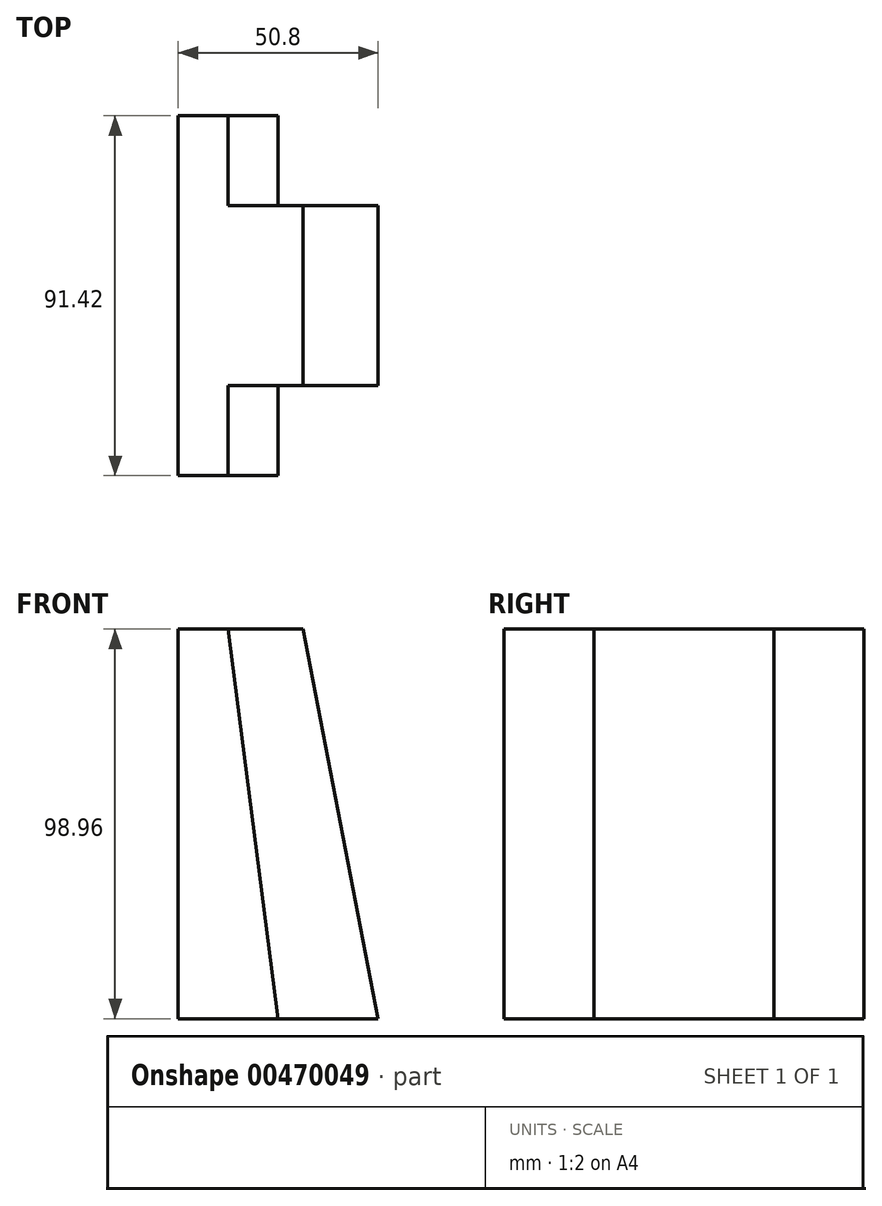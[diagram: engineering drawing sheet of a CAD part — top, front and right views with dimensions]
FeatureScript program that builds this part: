
annotation { "Feature Type Name" : "Feature", "Feature Type Description" : "" }
export const myFeature = defineFeature(function(context is Context, id is Id, definition is map)
    precondition{}
    {
        {
            var Q0;
            Q0=qCreatedBy(makeId("Right.planeOp"),FACE);
            var sketch = newSketch(context, id + "F0", { "sketchPlane" : qUnion([Q0])});
            skLineSegment(sketch, "E0", {"start": v(0, 0) * mm, "end": v(0, 49.48) * mm});
            skLineSegment(sketch, "E1", {"start": v(0, 49.48) * mm, "end": v(-45.7, 49.48) * mm});
            skLineSegment(sketch, "E2", {"start": v(-45.7, 49.48) * mm, "end": v(-45.7, -49.48) * mm});
            skLineSegment(sketch, "E3", {"start": v(-45.7, -49.48) * mm, "end": v(0, -49.48) * mm});
            skLineSegment(sketch, "E4", {"start": v(0, -49.48) * mm, "end": v(0, 0) * mm});
            skLineSegment(sketch, "E5", {"start": v(-22.85, 49.48) * mm, "end": v(-22.85, -49.48) * mm});
            skSolve(sketch);
        }
        {
            var Q0;
            {var subQ0=sQuery(id+"F0.wireOp",EDGE,"E2");Q0=makeQuery(id+"F0.imprint","IMPRINT",FACE,{"disambiguationData":[TD([[makeQuery(id+"F0.imprint","IMPRINT",EDGE,{"derivedFrom":subQ0}),1.0]])]});}
            extrude(context, id + "F1", {"entities" : qUnion([Q0]), "depth" : 25.4 * mm});
        }
        {
            var Q0;
            Q0=makeQuery(id+"F1.opExtrude","SWEPT_FACE",FACE,{"disambiguationData":[OSD([sQuery(id+"F0.wireOp",EDGE,"E2")])]});
            var sketch = newSketch(context, id + "F2", { "sketchPlane" : qUnion([Q0])});
            skLineSegment(sketch, "E6", {"start": v(12.7, 49.48) * mm, "end": v(25.4, -49.48) * mm});
            skLineSegment(sketch, "E7", {"start": v(25.4, -49.48) * mm, "end": v(25.4, 49.48) * mm});
            skLineSegment(sketch, "E8", {"start": v(25.4, 49.48) * mm, "end": v(12.7, 49.48) * mm});
            skSolve(sketch);
        }
        {
            var Q0;
            Q0 = qSketchRegion(id + "F2", true);
            extrude(context, id + "F3", {"entities" : qUnion([Q0]), "operationType" : NewBodyOperationType.REMOVE, "endBound" : BoundingType.THROUGH_ALL, "oppositeDirection" : true, "depth" : 25.4 * mm});
        }
        {
            var Q0;
            {var subQ2=sQuery(id+"F0.wireOp",EDGE,"E0");Q0=makeQuery(id+"F0.imprint","IMPRINT",FACE,{"disambiguationData":[TD([[makeQuery(id+"F0.imprint","IMPRINT",EDGE,{"derivedFrom":subQ2}),1.0]])]});}
            extrude(context, id + "F4", {"entities" : qUnion([Q0]), "operationType" : NewBodyOperationType.ADD, "depth" : 50.8 * mm});
        }
        {
            var Q0;
            Q0=makeQuery(id+"F4.opExtrude","SWEPT_FACE",FACE,{"disambiguationData":[OSD([sQuery(id+"F0.wireOp",EDGE,"E5")])]});
            var sketch = newSketch(context, id + "F5", { "sketchPlane" : qUnion([Q0])});
            skLineSegment(sketch, "E9", {"start": v(31.75, 49.48) * mm, "end": v(50.8, -49.48) * mm});
            skLineSegment(sketch, "E10", {"start": v(50.8, -49.48) * mm, "end": v(50.8, 49.48) * mm});
            skLineSegment(sketch, "E11", {"start": v(50.8, 49.48) * mm, "end": v(31.75, 49.48) * mm});
            skSolve(sketch);
        }
        {
            var Q0;
            Q0 = qSketchRegion(id + "F5", true);
            extrude(context, id + "F6", {"entities" : qUnion([Q0]), "operationType" : NewBodyOperationType.REMOVE, "endBound" : BoundingType.THROUGH_ALL, "oppositeDirection" : true, "depth" : 25.4 * mm});
        }
        {
            var Q0;
            Q0=makeQuery(id+"F1.opExtrude","SWEPT_BODY",BODY,{"disambiguationData":[OSD([sQuery(id+"F0.wireOp",EDGE,"E1"),sQuery(id+"F0.wireOp",EDGE,"E2"),sQuery(id+"F0.wireOp",EDGE,"E3"),sQuery(id+"F0.wireOp",EDGE,"E5")])]});
            var Q1;
            Q1=qCreatedBy(makeId("Front.planeOp"),FACE);
            mirror(context, id + "F7", {"operationType" : NewBodyOperationType.ADD, "entities" : qUnion([Q0]), "mirrorPlane" : qUnion([Q1])});
        }
    });
